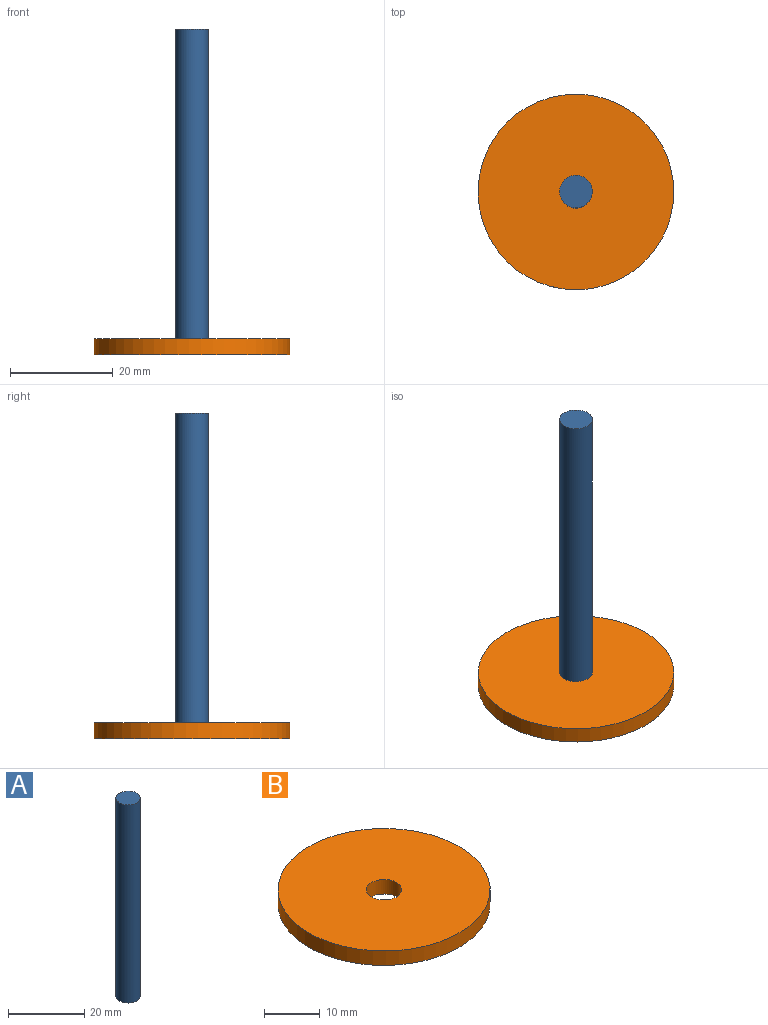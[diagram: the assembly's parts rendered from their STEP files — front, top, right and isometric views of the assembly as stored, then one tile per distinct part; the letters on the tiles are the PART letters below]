
ASSEMBLY  parts=2 mates=1
PART A: 3 faces, bbox 6.4x6.4x63.5 mm
  f0: plane 6.35x6.35mm, normal (0,0,1), area 31.7mm2, adj f1
  f1: cylinder r=3.17mm len=63.5mm, axis (0,0,-1), area 1266.8mm2, adj f0,f2
  f2: plane 6.35x6.35mm, normal (0,0,-1), area 31.7mm2, adj f1
PART B: 4 faces, bbox 38.1x38.1x3.2 mm
  f0: cylinder r=3.17mm len=6.35mm, axis (0,0,-1), area 63.3mm2, adj f2,f3
  f1: cylinder r=19.05mm len=38.1mm, axis (0,0,-1), area 380mm2, adj f2,f3
  f2: plane 38.1x38.1mm, normal (0,0,1), area 1108.4mm2, adj f0,f1
  f3: plane 38.1x38.1mm, normal (0,0,-1), area 1108.4mm2, adj f0,f1
PLACE A rot(axis=(0.74,-0.57,-0.37),0deg) t=(4.98,4.33,3.4)mm
PLACE B rot(axis=(0.74,-0.57,-0.37),0deg) t=(4.98,4.33,3.4)mm
MATE fastened A.f1 <-> B.f1  axis (0,0,-1) through (-64.87,4.33,73.25)mm
